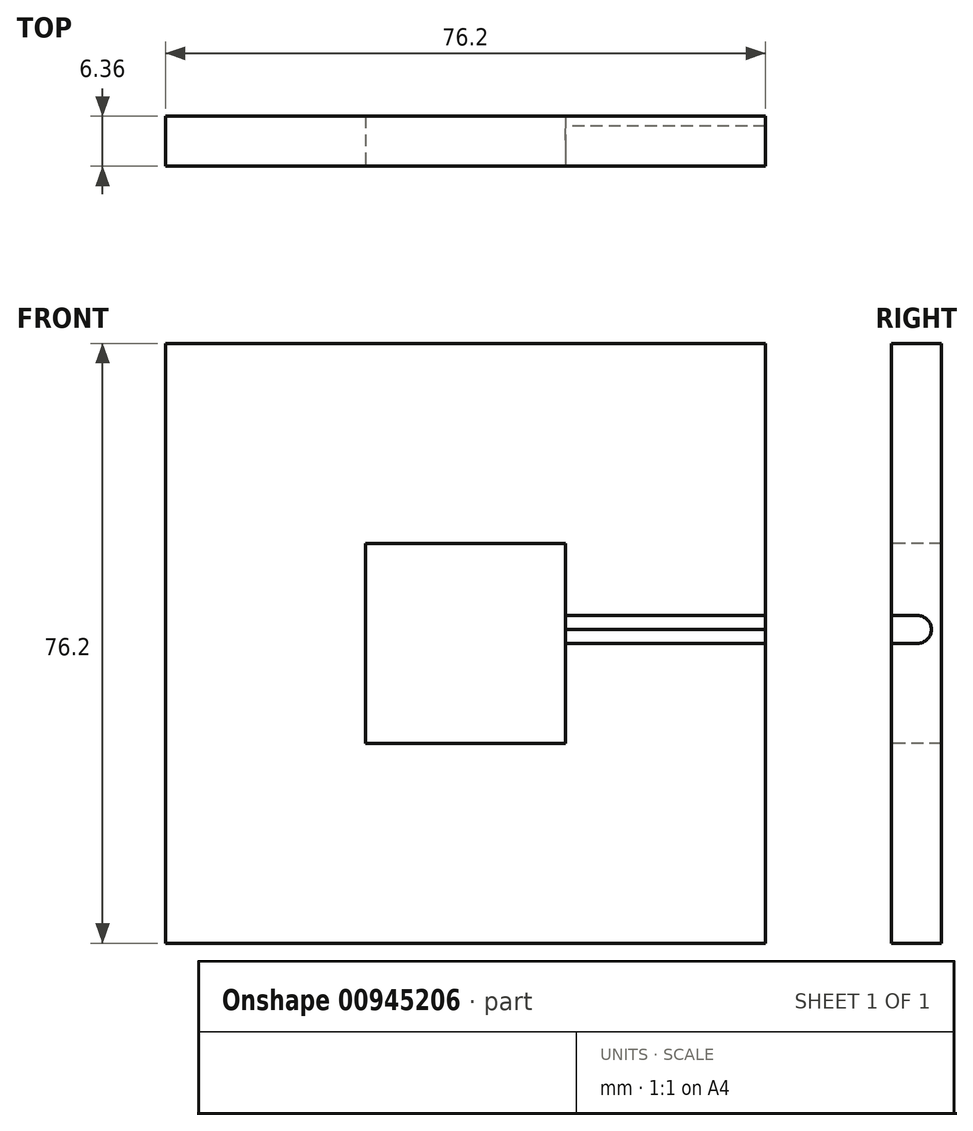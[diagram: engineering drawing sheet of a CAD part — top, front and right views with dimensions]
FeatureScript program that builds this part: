
annotation { "Feature Type Name" : "Feature", "Feature Type Description" : "" }
export const myFeature = defineFeature(function(context is Context, id is Id, definition is map)
    precondition{}
    {
        {
            var Q0;
            Q0=qCreatedBy(makeId("Top.planeOp"),FACE);
            var sketch = newSketch(context, id + "F0", { "sketchPlane" : qUnion([Q0])});
            skLineSegment(sketch, "E0.bottom", {"start": v(38.1, -3.18) * mm, "end": v(-38.1, -3.18) * mm});
            skLineSegment(sketch, "E0.top", {"start": v(38.1, 3.17) * mm, "end": v(-38.1, 3.17) * mm});
            skLineSegment(sketch, "E0.left", {"start": v(38.1, -3.18) * mm, "end": v(38.1, 3.17) * mm});
            skLineSegment(sketch, "E0.right", {"start": v(-38.1, -3.18) * mm, "end": v(-38.1, 3.17) * mm});
            skPoint(sketch, "E0.middle", {"position": v(0, 0) * mm});
            skSolve(sketch);
        }
        {
            var Q0;
            Q0=makeQuery(id+"F0.imprint","IMPRINT",FACE,{"disambiguationData":[TD([[makeQuery(id+"F0.imprint","IMPRINT",EDGE,{"derivedFrom":sQuery(id+"F0.wireOp",EDGE,"E0.bottom")}),-1.0]])]});
            extrude(context, id + "F1", {"entities" : qUnion([Q0]), "depth" : 76.2 * mm, "offsetDistance" : 25.4 * mm});
        }
        {
            var Q0;
            Q0=makeQuery(id+"F1.opExtrude","SWEPT_FACE",FACE,{"disambiguationData":[OSD([sQuery(id+"F0.wireOp",EDGE,"E0.bottom")])]});
            var sketch = newSketch(context, id + "F2", { "sketchPlane" : qUnion([Q0])});
            skLineSegment(sketch, "E1.bottom", {"start": v(12.7, 25.4) * mm, "end": v(-12.7, 25.4) * mm});
            skLineSegment(sketch, "E1.top", {"start": v(12.7, 50.8) * mm, "end": v(-12.7, 50.8) * mm});
            skLineSegment(sketch, "E1.left", {"start": v(12.7, 25.4) * mm, "end": v(12.7, 50.8) * mm});
            skLineSegment(sketch, "E1.right", {"start": v(-12.7, 25.4) * mm, "end": v(-12.7, 50.8) * mm});
            skPoint(sketch, "E1.middle", {"position": v(0, 38.1) * mm});
            skSolve(sketch);
        }
        {
            var Q0;
            Q0=makeQuery(id+"F2.imprint","IMPRINT",FACE,{"disambiguationData":[TD([[makeQuery(id+"F2.imprint","IMPRINT",EDGE,{"derivedFrom":sQuery(id+"F2.wireOp",EDGE,"E1.bottom")}),-1.0]])]});
            extrude(context, id + "F3", {"entities" : qUnion([Q0]), "operationType" : NewBodyOperationType.REMOVE, "oppositeDirection" : true, "depth" : 25.4 * mm, "offsetDistance" : 25.4 * mm});
        }
        {
            var Q0;
            Q0=makeQuery(id+"F1.opExtrude","SWEPT_FACE",FACE,{"disambiguationData":[OSD([sQuery(id+"F0.wireOp",EDGE,"E0.bottom")])]});
            var sketch = newSketch(context, id + "F4", { "sketchPlane" : qUnion([Q0])});
            skLineSegment(sketch, "E2.bottom", {"start": v(12.7, 41.63) * mm, "end": v(38.1, 41.63) * mm});
            skLineSegment(sketch, "E2.top", {"start": v(12.7, 38.1) * mm, "end": v(38.1, 38.1) * mm});
            skLineSegment(sketch, "E2.left", {"start": v(12.7, 41.63) * mm, "end": v(12.7, 38.1) * mm});
            skLineSegment(sketch, "E2.right", {"start": v(38.1, 41.63) * mm, "end": v(38.1, 38.1) * mm});
            skSolve(sketch);
        }
        {
            var Q0;
            Q0=makeQuery(id+"F4.imprint","IMPRINT",FACE,{"disambiguationData":[TD([[makeQuery(id+"F4.imprint","IMPRINT",EDGE,{"derivedFrom":sQuery(id+"F4.wireOp",EDGE,"E2.bottom")}),-1.0]])]});
            extrude(context, id + "F5", {"entities" : qUnion([Q0]), "operationType" : NewBodyOperationType.REMOVE, "oppositeDirection" : true, "depth" : 5.08 * mm, "offsetDistance" : 25.4 * mm});
        }
        {
            var Q0;
            Q0=makeQuery(id+"F5.boolean.opBoolean","COPY",FACE,{"derivedFrom":makeQuery(id+"F5.opExtrude","SWEPT_FACE",FACE,{"disambiguationData":[OSD([sQuery(id+"F4.wireOp",EDGE,"E2.top")])]})});
            var sketch = newSketch(context, id + "F6", { "sketchPlane" : qUnion([Q0])});
            skLineSegment(sketch, "E3.bottom", {"start": v(12.7, -3.18) * mm, "end": v(38.1, -3.18) * mm});
            skLineSegment(sketch, "E3.top", {"start": v(12.7, -2.5) * mm, "end": v(38.1, -2.5) * mm});
            skLineSegment(sketch, "E3.left", {"start": v(12.7, -3.18) * mm, "end": v(12.7, -2.5) * mm});
            skLineSegment(sketch, "E3.right", {"start": v(38.1, -3.18) * mm, "end": v(38.1, -2.5) * mm});
            skSolve(sketch);
        }
        {
            var Q0;
            Q0 = qConstructionFilter(qBodyType(qCreatedBy(id + "F6" ,EDGE), BodyType.WIRE), ConstructionObject.NO);
            extrude(context, id + "F7", {"bodyType" : ToolBodyType.SURFACE, "surfaceEntities" : qUnion([Q0]), "depth" : 3.53 * mm, "offsetDistance" : 25.4 * mm});
        }
        {
            var Q0;
            Q0=makeQuery(id+"F5.boolean.opBoolean","COPY",EDGE,{"derivedFrom":makeQuery(id+"F5.opExtrude","CAP_EDGE",EDGE,{"disambiguationData":[OSD([sQuery(id+"F4.wireOp",EDGE,"E2.bottom")])],"isStart":false})});
            var Q1;
            Q1=makeQuery(id+"F5.boolean.opBoolean","COPY",EDGE,{"derivedFrom":makeQuery(id+"F5.opExtrude","CAP_EDGE",EDGE,{"disambiguationData":[OSD([sQuery(id+"F4.wireOp",EDGE,"E2.top")])],"isStart":false})});
            fillet(context, id + "F8", {"entities" : qUnion([Q0, Q1]), "radius" : 1.78 * mm, "tangentPropagation" : true, "allowEdgeOverflow" : false});
        }
    });
